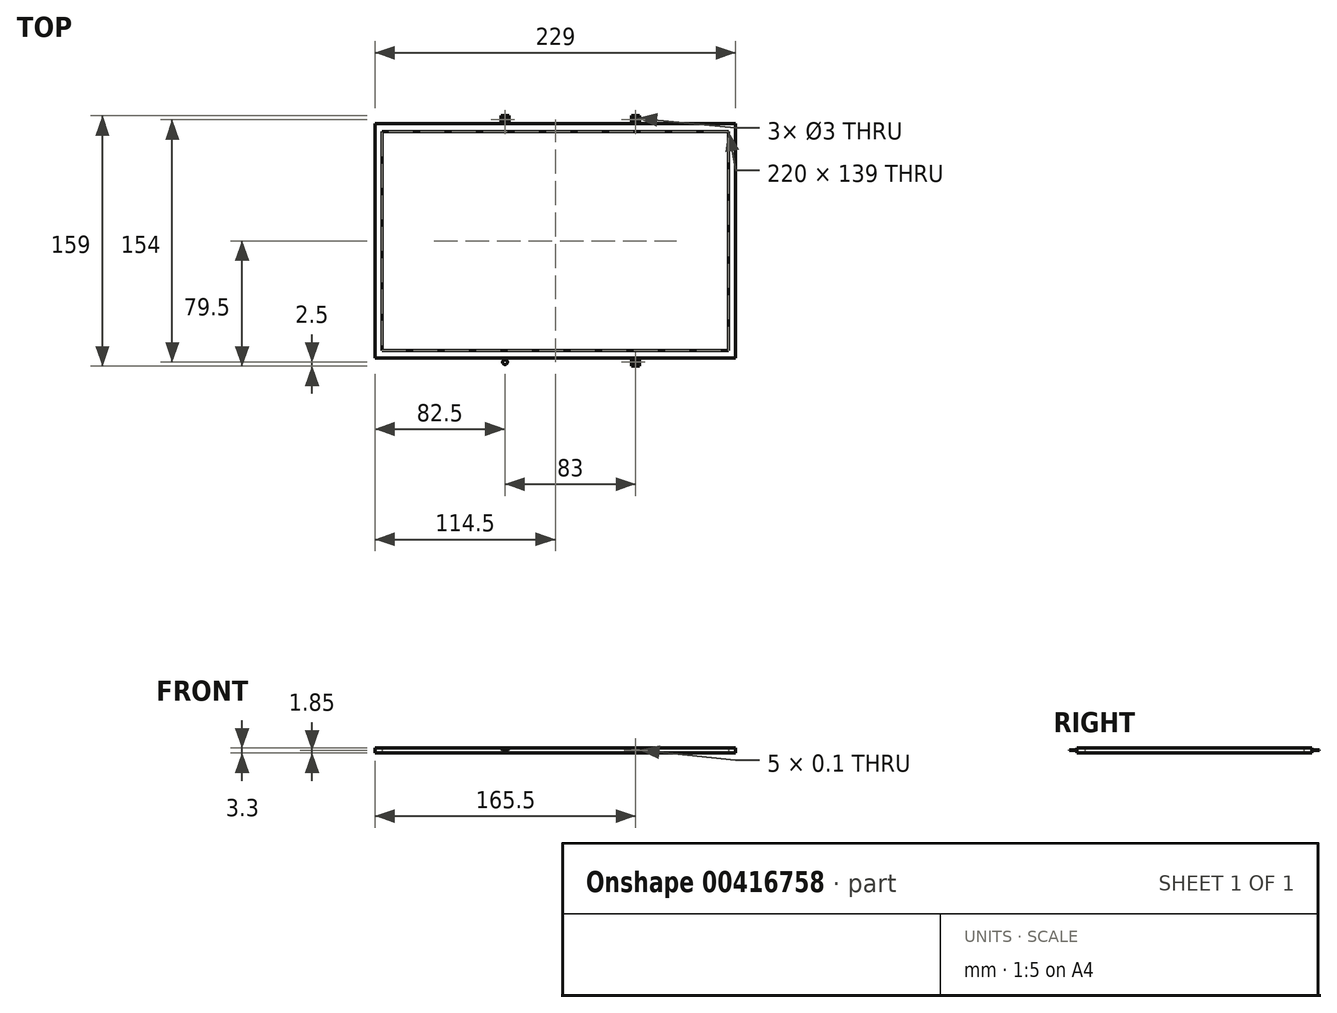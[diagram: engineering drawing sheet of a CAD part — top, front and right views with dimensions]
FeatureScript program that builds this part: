
annotation { "Feature Type Name" : "Feature", "Feature Type Description" : "" }
export const myFeature = defineFeature(function(context is Context, id is Id, definition is map)
    precondition{}
    {
        {
            var Q0;
            Q0=qCreatedBy(makeId("Top.planeOp"),FACE);
            var sketch = newSketch(context, id + "F0", { "sketchPlane" : qUnion([Q0])});
            skLineSegment(sketch, "E0.bottom", {"start": v(0, 0) * mm, "end": v(229, 0) * mm});
            skLineSegment(sketch, "E0.top", {"start": v(0, -149) * mm, "end": v(229, -149) * mm});
            skLineSegment(sketch, "E0.left", {"start": v(0, 0) * mm, "end": v(0, -149) * mm});
            skLineSegment(sketch, "E0.right", {"start": v(229, 0) * mm, "end": v(229, -149) * mm});
            skLineSegment(sketch, "E1.0", {"start": v(4.5, -5) * mm, "end": v(224.5, -5) * mm});
            skLineSegment(sketch, "E2.0", {"start": v(4.5, -144) * mm, "end": v(224.5, -144) * mm});
            skLineSegment(sketch, "E3.0", {"start": v(4.5, -5) * mm, "end": v(4.5, -144) * mm});
            skLineSegment(sketch, "E4.0", {"start": v(224.5, -5) * mm, "end": v(224.5, -144) * mm});
            skSolve(sketch);
        }
        {
            var Q0;
            Q0=makeQuery(id+"F0.imprint","IMPRINT",FACE,{"disambiguationData":[TD([[makeQuery(id+"F0.imprint","IMPRINT",EDGE,{"derivedFrom":sQuery(id+"F0.wireOp",EDGE,"E0.bottom")}),-1.0]])]});
            extrude(context, id + "F1", {"entities" : qUnion([Q0]), "depth" : 3.3 * mm});
        }
        {
            var Q0;
            Q0=qCreatedBy(makeId("Top.planeOp"),FACE);
            cPlane(context, id + "F2", {"entities" : qUnion([Q0]), "cplaneType" : CPlaneType.OFFSET, "offset" : 1.8 * mm, "width" : 150 * mm, "height" : 150 * mm});
        }
        {
            var Q0;
            Q0=qCreatedBy(id+"F2.planeOp",FACE);
            var sketch = newSketch(context, id + "F3", { "sketchPlane" : qUnion([Q0])});
            skLineSegment(sketch, "E5.bottom", {"start": v(163, 0) * mm, "end": v(168, 0) * mm});
            skLineSegment(sketch, "E5.top", {"start": v(163, 5) * mm, "end": v(168, 5) * mm});
            skLineSegment(sketch, "E5.left", {"start": v(163, 0) * mm, "end": v(163, 5) * mm});
            skLineSegment(sketch, "E5.right", {"start": v(168, 0) * mm, "end": v(168, 5) * mm});
            skCircle(sketch, "E6", {"center": v(165.5, 2.5) * mm, "radius": 1.5 * mm});
            skPoint(sketch, "E6.centerSnap0", {"position": v(165.5, 5) * mm});
            skPoint(sketch, "E6.centerSnap1", {"position": v(163, 2.5) * mm});
            skPoint(sketch, "E7.MirrorP", {"position": v(80, -151.5) * mm});
            skPoint(sketch, "E8.MirrorP", {"position": v(82.5, -154) * mm});
            skCircle(sketch, "E9.MirrorC", {"center": v(82.5, -151.5) * mm, "radius": 1.5 * mm});
            skLineSegment(sketch, "E10.MirrorCS", {"start": v(85, -149) * mm, "end": v(85, -154) * mm});
            skLineSegment(sketch, "E11.MirrorCS", {"start": v(80, -149) * mm, "end": v(80, -154) * mm});
            skLineSegment(sketch, "E12.MirrorCS", {"start": v(80, -154) * mm, "end": v(85, -154) * mm});
            skLineSegment(sketch, "E13.MirrorCS", {"start": v(80, -149) * mm, "end": v(85, -149) * mm});
            skLineSegment(sketch, "E14.MirrorCS", {"start": v(163, -154) * mm, "end": v(168, -154) * mm});
            skLineSegment(sketch, "E15.MirrorCS", {"start": v(163, -149) * mm, "end": v(163, -154) * mm});
            skPoint(sketch, "E16.MirrorP", {"position": v(165.5, -154) * mm});
            skLineSegment(sketch, "E17.MirrorCS", {"start": v(163, -149) * mm, "end": v(168, -149) * mm});
            skLineSegment(sketch, "E18.MirrorCS", {"start": v(168, -149) * mm, "end": v(168, -154) * mm});
            skCircle(sketch, "E19.MirrorC", {"center": v(165.5, -151.5) * mm, "radius": 1.5 * mm});
            skPoint(sketch, "E20.MirrorP", {"position": v(163, -151.5) * mm});
            skLineSegment(sketch, "E21", {"start": v(0, 0) * mm, "end": v(80, 0) * mm});
            skLineSegment(sketch, "E22.bottom", {"start": v(80, 0) * mm, "end": v(85, 0) * mm});
            skLineSegment(sketch, "E22.top", {"start": v(80, 5) * mm, "end": v(85, 5) * mm});
            skLineSegment(sketch, "E22.left", {"start": v(80, 0) * mm, "end": v(80, 5) * mm});
            skLineSegment(sketch, "E23", {"start": v(85, 5) * mm, "end": v(85, 0) * mm});
            skCircle(sketch, "E24", {"center": v(82.5, 2.5) * mm, "radius": 1.5 * mm});
            skPoint(sketch, "E24.centerSnap0", {"position": v(82.5, 5) * mm});
            skPoint(sketch, "E24.centerSnap1", {"position": v(80, 2.5) * mm});
            skSolve(sketch);
        }
        {
            var Q0;
            Q0=makeQuery(id+"F3.imprint","IMPRINT",FACE,{"disambiguationData":[TD([[makeQuery(id+"F3.imprint","IMPRINT",EDGE,{"derivedFrom":sQuery(id+"F3.wireOp",EDGE,"QukOBhhz-5grh-USXH-mB6t-flz0tiGGflIy.bottom")}),1.0]])]});
            var Q1;
            Q1=makeQuery(id+"F3.imprint","IMPRINT",FACE,{"disambiguationData":[TD([[makeQuery(id+"F3.imprint","IMPRINT",EDGE,{"derivedFrom":sQuery(id+"F3.wireOp",EDGE,"E5.bottom")}),1.0]])]});
            var Q2;
            Q2=makeQuery(id+"F3.imprint","IMPRINT",FACE,{"disambiguationData":[TD([[makeQuery(id+"F3.imprint","IMPRINT",EDGE,{"derivedFrom":sQuery(id+"F3.wireOp",EDGE,"E9.MirrorC")}),1.0]])]});
            var Q3;
            Q3=makeQuery(id+"F3.imprint","IMPRINT",FACE,{"disambiguationData":[TD([[makeQuery(id+"F3.imprint","IMPRINT",EDGE,{"derivedFrom":sQuery(id+"F3.wireOp",EDGE,"E14.MirrorCS")}),1.0]])]});
            var Q4;
            Q4=makeQuery(id+"F3.imprint","IMPRINT",FACE,{"disambiguationData":[TD([[makeQuery(id+"F3.imprint","IMPRINT",EDGE,{"derivedFrom":sQuery(id+"F3.wireOp",EDGE,"E22.bottom")}),1.0]])]});
            extrude(context, id + "F4", {"entities" : qUnion([Q0, Q1, Q2, Q3, Q4]), "operationType" : NewBodyOperationType.ADD, "depth" : 0.1 * mm});
        }
    });
